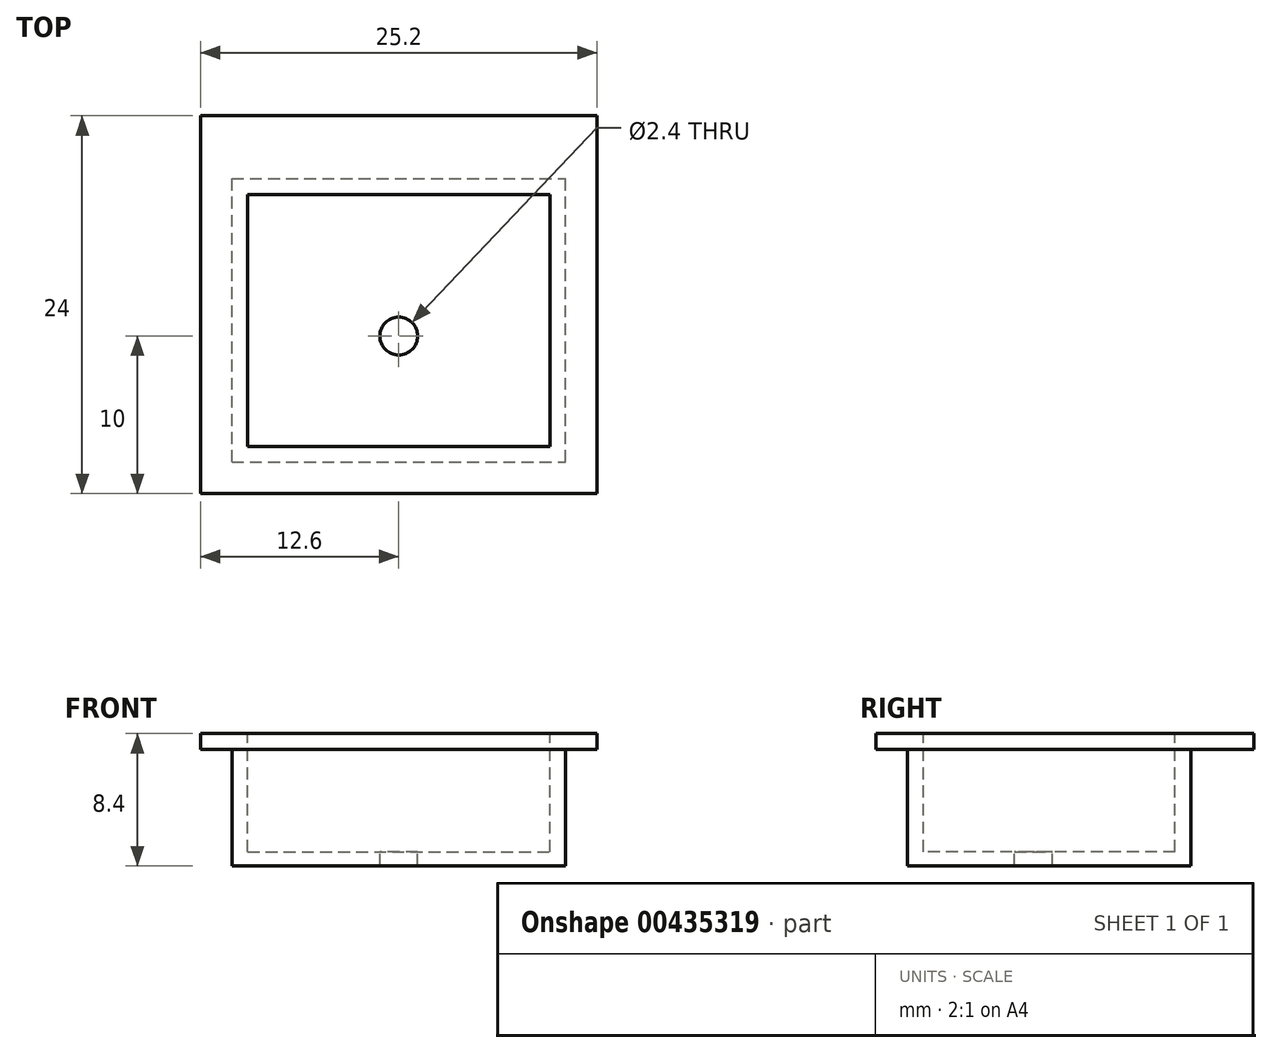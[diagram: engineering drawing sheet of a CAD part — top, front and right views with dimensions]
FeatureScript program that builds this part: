
annotation { "Feature Type Name" : "Feature", "Feature Type Description" : "" }
export const myFeature = defineFeature(function(context is Context, id is Id, definition is map)
    precondition{}
    {
        {
            var Q0;
            Q0=qCreatedBy(makeId("Top.planeOp"),FACE);
            var sketch = newSketch(context, id + "F0", { "sketchPlane" : qUnion([Q0])});
            skLineSegment(sketch, "E0.bottom", {"start": v(0, 0) * mm, "end": v(21.2, 0) * mm});
            skLineSegment(sketch, "E0.top", {"start": v(0, 18) * mm, "end": v(21.2, 18) * mm});
            skLineSegment(sketch, "E0.left", {"start": v(0, 0) * mm, "end": v(0, 18) * mm});
            skLineSegment(sketch, "E0.right", {"start": v(21.2, 0) * mm, "end": v(21.2, 18) * mm});
            skSolve(sketch);
        }
        {
            var Q0;
            Q0=makeQuery(id+"F0.imprint","IMPRINT",FACE,{"disambiguationData":[TD([[makeQuery(id+"F0.imprint","IMPRINT",EDGE,{"derivedFrom":sQuery(id+"F0.wireOp",EDGE,"E0.bottom")}),1.0]])]});
            extrude(context, id + "F1", {"entities" : qUnion([Q0]), "depth" : 8.4 * mm});
        }
        {
            var Q0;
            Q0=makeQuery(id+"F1.opExtrude","CAP_FACE",FACE,{"disambiguationData":[OSD([sQuery(id+"F0.wireOp",EDGE,"E0.bottom"),sQuery(id+"F0.wireOp",EDGE,"E0.top"),sQuery(id+"F0.wireOp",EDGE,"E0.left"),sQuery(id+"F0.wireOp",EDGE,"E0.right")])],"isStart":false});
            var sketch = newSketch(context, id + "F2", { "sketchPlane" : qUnion([Q0])});
            skLineSegment(sketch, "E1.bottom", {"start": v(1, 17) * mm, "end": v(20.2, 17) * mm});
            skLineSegment(sketch, "E1.top", {"start": v(1, 1) * mm, "end": v(20.2, 1) * mm});
            skLineSegment(sketch, "E1.left", {"start": v(1, 17) * mm, "end": v(1, 1) * mm});
            skLineSegment(sketch, "E1.right", {"start": v(20.2, 17) * mm, "end": v(20.2, 1) * mm});
            skSolve(sketch);
        }
        {
            var Q0;
            Q0=makeQuery(id+"F2.imprint","IMPRINT",FACE,{"disambiguationData":[TD([[makeQuery(id+"F2.imprint","IMPRINT",EDGE,{"derivedFrom":sQuery(id+"F2.wireOp",EDGE,"E1.bottom")}),-1.0]])]});
            extrude(context, id + "F3", {"entities" : qUnion([Q0]), "operationType" : NewBodyOperationType.REMOVE, "oppositeDirection" : true, "depth" : 7.5 * mm});
        }
        {
            var Q0;
            Q0=makeQuery(id+"F1.opExtrude","CAP_FACE",FACE,{"disambiguationData":[OSD([sQuery(id+"F0.wireOp",EDGE,"E0.bottom"),sQuery(id+"F0.wireOp",EDGE,"E0.top"),sQuery(id+"F0.wireOp",EDGE,"E0.left"),sQuery(id+"F0.wireOp",EDGE,"E0.right")])],"isStart":false});
            var sketch = newSketch(context, id + "F4", { "sketchPlane" : qUnion([Q0])});
            skLineSegment(sketch, "E2.bottom", {"start": v(0, 18) * mm, "end": v(21.2, 18) * mm});
            skLineSegment(sketch, "E2.top", {"start": v(-2, 22) * mm, "end": v(23.2, 22) * mm});
            skLineSegment(sketch, "E3", {"start": v(-2, 22) * mm, "end": v(-2, -2) * mm});
            skLineSegment(sketch, "E4", {"start": v(-2, -2) * mm, "end": v(23.2, -2) * mm});
            skLineSegment(sketch, "E5", {"start": v(23.2, -2) * mm, "end": v(23.2, 22) * mm});
            skLineSegment(sketch, "E6", {"start": v(0, 18) * mm, "end": v(0, 0) * mm});
            skLineSegment(sketch, "E7", {"start": v(0, 0) * mm, "end": v(21.2, 0) * mm});
            skLineSegment(sketch, "E8", {"start": v(21.2, 0) * mm, "end": v(21.2, 18) * mm});
            skSolve(sketch);
        }
        {
            var Q0;
            Q0=makeQuery(id+"F4.imprint","IMPRINT",FACE,{"disambiguationData":[TD([[makeQuery(id+"F4.imprint","IMPRINT",EDGE,{"derivedFrom":sQuery(id+"F4.wireOp",EDGE,"E2.bottom")}),1.0]])]});
            extrude(context, id + "F5", {"entities" : qUnion([Q0]), "operationType" : NewBodyOperationType.ADD, "oppositeDirection" : true, "depth" : 1 * mm});
        }
        {
            var Q0;
            Q0=makeQuery(id+"F3.boolean.opBoolean","COPY",FACE,{"derivedFrom":makeQuery(id+"F3.opExtrude","CAP_FACE",FACE,{"disambiguationData":[OSD([sQuery(id+"F2.wireOp",EDGE,"E1.bottom"),sQuery(id+"F2.wireOp",EDGE,"E1.top"),sQuery(id+"F2.wireOp",EDGE,"E1.left"),sQuery(id+"F2.wireOp",EDGE,"E1.right")])],"isStart":false})});
            var sketch = newSketch(context, id + "F6", { "sketchPlane" : qUnion([Q0])});
            skCircle(sketch, "E9", {"center": v(10.6, 8) * mm, "radius": 1.2 * mm});
            skSolve(sketch);
        }
        {
            var Q0;
            Q0=makeQuery(id+"F6.imprint","IMPRINT",FACE,{"disambiguationData":[TD([[makeQuery(id+"F6.imprint","IMPRINT",EDGE,{"derivedFrom":sQuery(id+"F6.wireOp",EDGE,"E9")}),1.0]])]});
            extrude(context, id + "F7", {"entities" : qUnion([Q0]), "operationType" : NewBodyOperationType.REMOVE, "endBound" : BoundingType.THROUGH_ALL, "oppositeDirection" : true, "depth" : 25 * mm});
        }
    });
